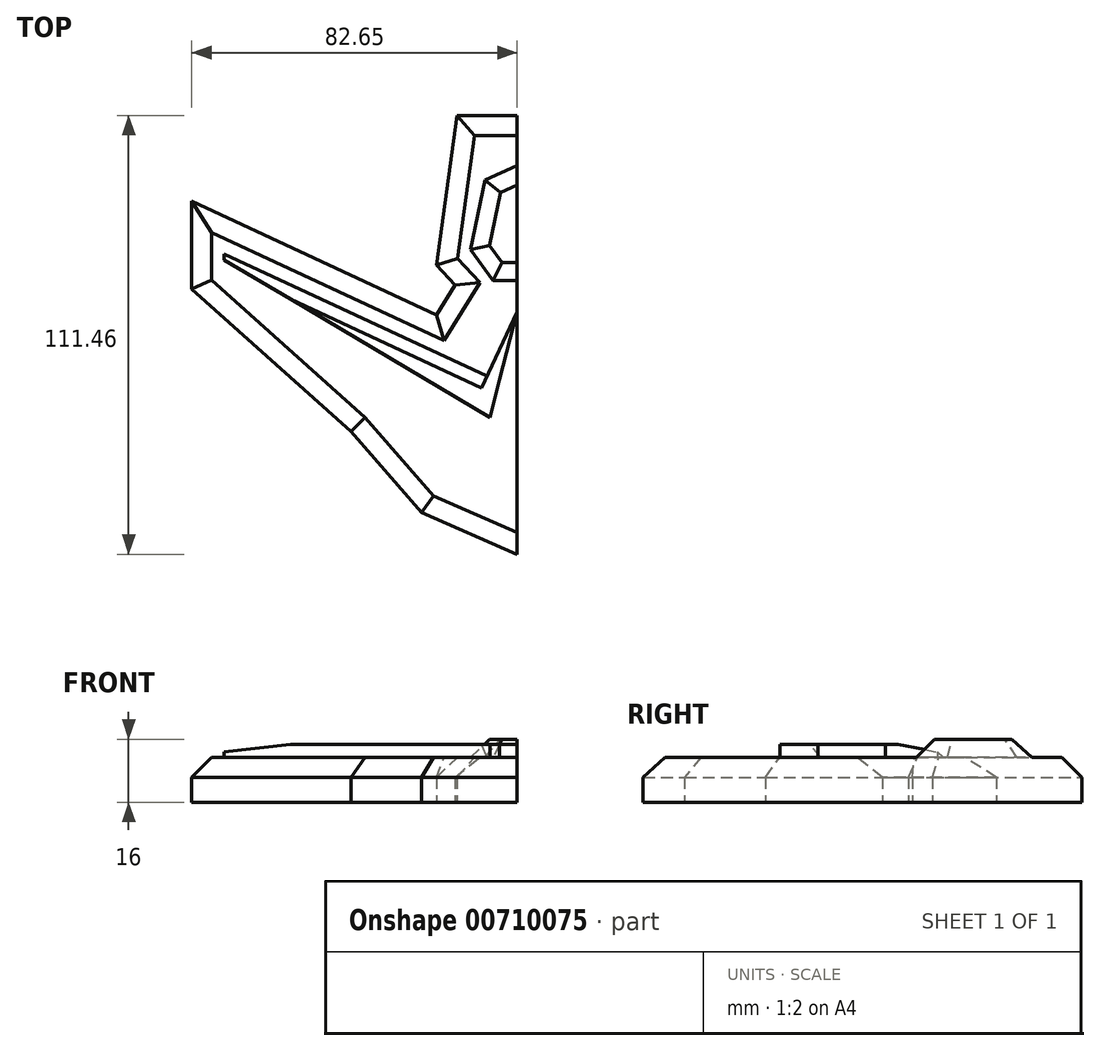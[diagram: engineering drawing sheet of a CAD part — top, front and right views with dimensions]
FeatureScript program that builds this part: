
annotation { "Feature Type Name" : "Feature", "Feature Type Description" : "" }
export const myFeature = defineFeature(function(context is Context, id is Id, definition is map)
    precondition{}
    {
        {
            var Q0;
            Q0=qCreatedBy(makeId("Top.planeOp"),FACE);
            var sketch = newSketch(context, id + "F0", { "sketchPlane" : qUnion([Q0])});
            skLineSegment(sketch, "E0", {"start": v(0, 64.61) * mm, "end": v(-15.2, 64.61) * mm});
            skLineSegment(sketch, "E1", {"start": v(-15.2, 64.61) * mm, "end": v(-20.5, 26.64) * mm});
            skLineSegment(sketch, "E2", {"start": v(-20.5, 26.64) * mm, "end": v(-15.78, 21.54) * mm});
            skLineSegment(sketch, "E3", {"start": v(-15.78, 21.54) * mm, "end": v(-20.5, 13.98) * mm});
            skLineSegment(sketch, "E4", {"start": v(-20.5, 13.98) * mm, "end": v(-82.65, 42.89) * mm});
            skLineSegment(sketch, "E5", {"start": v(-82.65, 42.89) * mm, "end": v(-82.65, 20.6) * mm});
            skLineSegment(sketch, "E6", {"start": v(-82.65, 20.6) * mm, "end": v(-42.22, -15.68) * mm});
            skLineSegment(sketch, "E7", {"start": v(-42.22, -15.68) * mm, "end": v(-24.28, -36.27) * mm});
            skLineSegment(sketch, "E8", {"start": v(-24.28, -36.27) * mm, "end": v(0, -46.85) * mm});
            skLineSegment(sketch, "E9", {"start": v(0, 64.61) * mm, "end": v(0, -46.85) * mm});
            skSolve(sketch);
        }
        {
            var Q0;
            Q0=makeQuery(id+"F0.imprint","IMPRINT",FACE,{"disambiguationData":[TD([[makeQuery(id+"F0.imprint","IMPRINT",EDGE,{"derivedFrom":sQuery(id+"F0.wireOp",EDGE,"E0")}),1.0]])]});
            extrude(context, id + "F1", {"entities" : qUnion([Q0]), "depth" : 11.43 * mm, "offsetDistance" : 25.4 * mm});
        }
        {
            var Q0;
            Q0=makeQuery(id+"F1.opExtrude","CAP_EDGE",EDGE,{"disambiguationData":[OSD([sQuery(id+"F0.wireOp",EDGE,"E4")])],"isStart":false});
            var Q1;
            Q1=makeQuery(id+"F1.opExtrude","CAP_EDGE",EDGE,{"disambiguationData":[OSD([sQuery(id+"F0.wireOp",EDGE,"E5")])],"isStart":false});
            var Q2;
            Q2=makeQuery(id+"F1.opExtrude","CAP_EDGE",EDGE,{"disambiguationData":[OSD([sQuery(id+"F0.wireOp",EDGE,"E6")])],"isStart":false});
            var Q3;
            Q3=makeQuery(id+"F1.opExtrude","CAP_EDGE",EDGE,{"disambiguationData":[OSD([sQuery(id+"F0.wireOp",EDGE,"E3")])],"isStart":false});
            var Q4;
            Q4=makeQuery(id+"F1.opExtrude","CAP_EDGE",EDGE,{"disambiguationData":[OSD([sQuery(id+"F0.wireOp",EDGE,"E2")])],"isStart":false});
            var Q5;
            Q5=makeQuery(id+"F1.opExtrude","CAP_EDGE",EDGE,{"disambiguationData":[OSD([sQuery(id+"F0.wireOp",EDGE,"E1")])],"isStart":false});
            var Q6;
            Q6=makeQuery(id+"F1.opExtrude","CAP_EDGE",EDGE,{"disambiguationData":[OSD([sQuery(id+"F0.wireOp",EDGE,"E0")])],"isStart":false});
            var Q7;
            Q7=makeQuery(id+"F1.opExtrude","CAP_EDGE",EDGE,{"disambiguationData":[OSD([sQuery(id+"F0.wireOp",EDGE,"E7")])],"isStart":false});
            var Q8;
            Q8=makeQuery(id+"F1.opExtrude","CAP_EDGE",EDGE,{"disambiguationData":[OSD([sQuery(id+"F0.wireOp",EDGE,"E8")])],"isStart":false});
            chamfer(context, id + "F2", {"entities" : qUnion([Q0, Q1, Q2, Q3, Q4, Q5, Q6, Q7, Q8]), "width" : 5.08 * mm, "tangentPropagation" : true});
        }
        {
            var Q0;
            Q0=makeQuery(id+"F1.opExtrude","CAP_FACE",FACE,{"disambiguationData":[OSD([sQuery(id+"F0.wireOp",EDGE,"E0"),sQuery(id+"F0.wireOp",EDGE,"E1"),sQuery(id+"F0.wireOp",EDGE,"E2"),sQuery(id+"F0.wireOp",EDGE,"E3"),sQuery(id+"F0.wireOp",EDGE,"E4"),sQuery(id+"F0.wireOp",EDGE,"E5"),sQuery(id+"F0.wireOp",EDGE,"E6"),sQuery(id+"F0.wireOp",EDGE,"E7"),sQuery(id+"F0.wireOp",EDGE,"E8"),sQuery(id+"F0.wireOp",EDGE,"E9")])],"isStart":false});
            var sketch = newSketch(context, id + "F3", { "sketchPlane" : qUnion([Q0])});
            skLineSegment(sketch, "E10", {"start": v(0, 52.52) * mm, "end": v(-8.61, 48.55) * mm});
            skLineSegment(sketch, "E11", {"start": v(-8.61, 48.55) * mm, "end": v(-12.4, 30.42) * mm});
            skLineSegment(sketch, "E12", {"start": v(-12.4, 30.42) * mm, "end": v(-6.34, 22.14) * mm});
            skLineSegment(sketch, "E13", {"start": v(-6.34, 22.14) * mm, "end": v(0, 22.14) * mm});
            skLineSegment(sketch, "E14", {"start": v(0, 22.14) * mm, "end": v(0, 52.52) * mm});
            skSolve(sketch);
        }
        {
            var Q0;
            Q0 = qSketchRegion(id + "F3", true);
            extrude(context, id + "F4", {"entities" : qUnion([Q0]), "operationType" : NewBodyOperationType.ADD, "depth" : 4.57 * mm, "offsetDistance" : 25.4 * mm});
        }
        {
            var Q0;
            Q0=makeQuery(id+"F4.opExtrude","CAP_EDGE",EDGE,{"disambiguationData":[OSD([sQuery(id+"F3.wireOp",EDGE,"E10")])],"isStart":false});
            var Q1;
            Q1=makeQuery(id+"F4.opExtrude","CAP_EDGE",EDGE,{"disambiguationData":[OSD([sQuery(id+"F3.wireOp",EDGE,"E11")])],"isStart":false});
            var Q2;
            Q2=makeQuery(id+"F4.opExtrude","CAP_EDGE",EDGE,{"disambiguationData":[OSD([sQuery(id+"F3.wireOp",EDGE,"E12")])],"isStart":false});
            var Q3;
            Q3=makeQuery(id+"F4.opExtrude","CAP_EDGE",EDGE,{"disambiguationData":[OSD([sQuery(id+"F3.wireOp",EDGE,"E13")])],"isStart":false});
            chamfer(context, id + "F5", {"entities" : qUnion([Q0, Q1, Q2, Q3]), "width" : 5.08 * mm, "tangentPropagation" : true});
        }
        {
            var Q0;
            Q0=makeQuery(id+"F1.opExtrude","CAP_FACE",FACE,{"disambiguationData":[OSD([sQuery(id+"F0.wireOp",EDGE,"E0"),sQuery(id+"F0.wireOp",EDGE,"E1"),sQuery(id+"F0.wireOp",EDGE,"E2"),sQuery(id+"F0.wireOp",EDGE,"E3"),sQuery(id+"F0.wireOp",EDGE,"E4"),sQuery(id+"F0.wireOp",EDGE,"E5"),sQuery(id+"F0.wireOp",EDGE,"E6"),sQuery(id+"F0.wireOp",EDGE,"E7"),sQuery(id+"F0.wireOp",EDGE,"E8"),sQuery(id+"F0.wireOp",EDGE,"E9")])],"isStart":false});
            var sketch = newSketch(context, id + "F6", { "sketchPlane" : qUnion([Q0])});
            skLineSegment(sketch, "E15", {"start": v(0, 14.74) * mm, "end": v(-6.85, 0) * mm});
            skLineSegment(sketch, "E16", {"start": v(-6.85, 0) * mm, "end": v(-74.38, 31.4) * mm});
            skLineSegment(sketch, "E17", {"start": v(-74.38, 31.4) * mm, "end": v(-74.38, 27.96) * mm});
            skLineSegment(sketch, "E18", {"start": v(-74.38, 27.96) * mm, "end": v(-6.85, -12.1) * mm});
            skLineSegment(sketch, "E19", {"start": v(-6.85, -12.1) * mm, "end": v(-4.46, -2.46) * mm});
            skLineSegment(sketch, "E20", {"start": v(-4.46, -2.46) * mm, "end": v(0, 14.74) * mm});
            skSolve(sketch);
        }
        {
            var Q0;
            Q0 = qSketchRegion(id + "F6", true);
            extrude(context, id + "F7", {"entities" : qUnion([Q0]), "operationType" : NewBodyOperationType.ADD, "depth" : 3.3 * mm, "offsetDistance" : 25.4 * mm});
        }
        {
            var Q0;
            Q0=makeQuery(id+"F7.opExtrude","CAP_EDGE",EDGE,{"disambiguationData":[OSD([sQuery(id+"F6.wireOp",EDGE,"E16")])],"isStart":false});
            chamfer(context, id + "F8", {"entities" : qUnion([Q0]), "width" : 5.08 * mm, "tangentPropagation" : true});
        }
    });
